# Revit family: Małkowski Martech_Brama_Marc-KDS - oparta na ścianie
name_source: partatom
category: Drzwi
units: mm (PartAtom-declared; Revit-internal decimal feet)

## family parameters
Numer OmniClass = 23.30.10.00
Obiekt nadrzędny = Ściana
Punkt obliczania pomieszczeń = Tak
Tnij formami wycięć po wczytaniu = Nie
Tytuł OmniClass = Doors
Współdzielony = Nie
Zawsze pionowo = Tak

## types (1)
- Kaseta wału do stropu bezpośrednio
    Elementy mocujące = kątownik stalowy 50x50x6 i płaskownik 40x3 z blachy stalowej, mocowanie śrubami sześciokątnymi M6x25 i kotwami stalowymi M10
    Funkcja = Wewnętrzna
    IfcExportAs = IfcDoor
    Model = Marc - KDS
    Obraz typu = 062-700x600-px-scale-730-547.jpg
    Odporność ogniowa = D, DH
    Producent = Małkowski - Martech S.A.
    Płaszcz kurtyny = niepalna tkanina z włókna szklanego, standardowo w kolorze szaro-srebrnym, z listwą obciążeniową zamocowanej do dolnej krawędzi płaszcza
    Szerokość = 0 mm  [stored 0 ft]
    Typ budowy = Kurtyna dymowa stała
    URL = https://www.malkowski.pl
    Wysokość = 0 mm  [stored 0 ft]
    Zakończenie ściany = Wg obiektu nadrzędnego

note: [stored X ft] marks values corroborated as IEEE doubles in the binary element streams (Revit-internal decimal feet)

## geometry (parser evidence)
native form markers: Blend x2
no freeform markers — native parametric forms only
